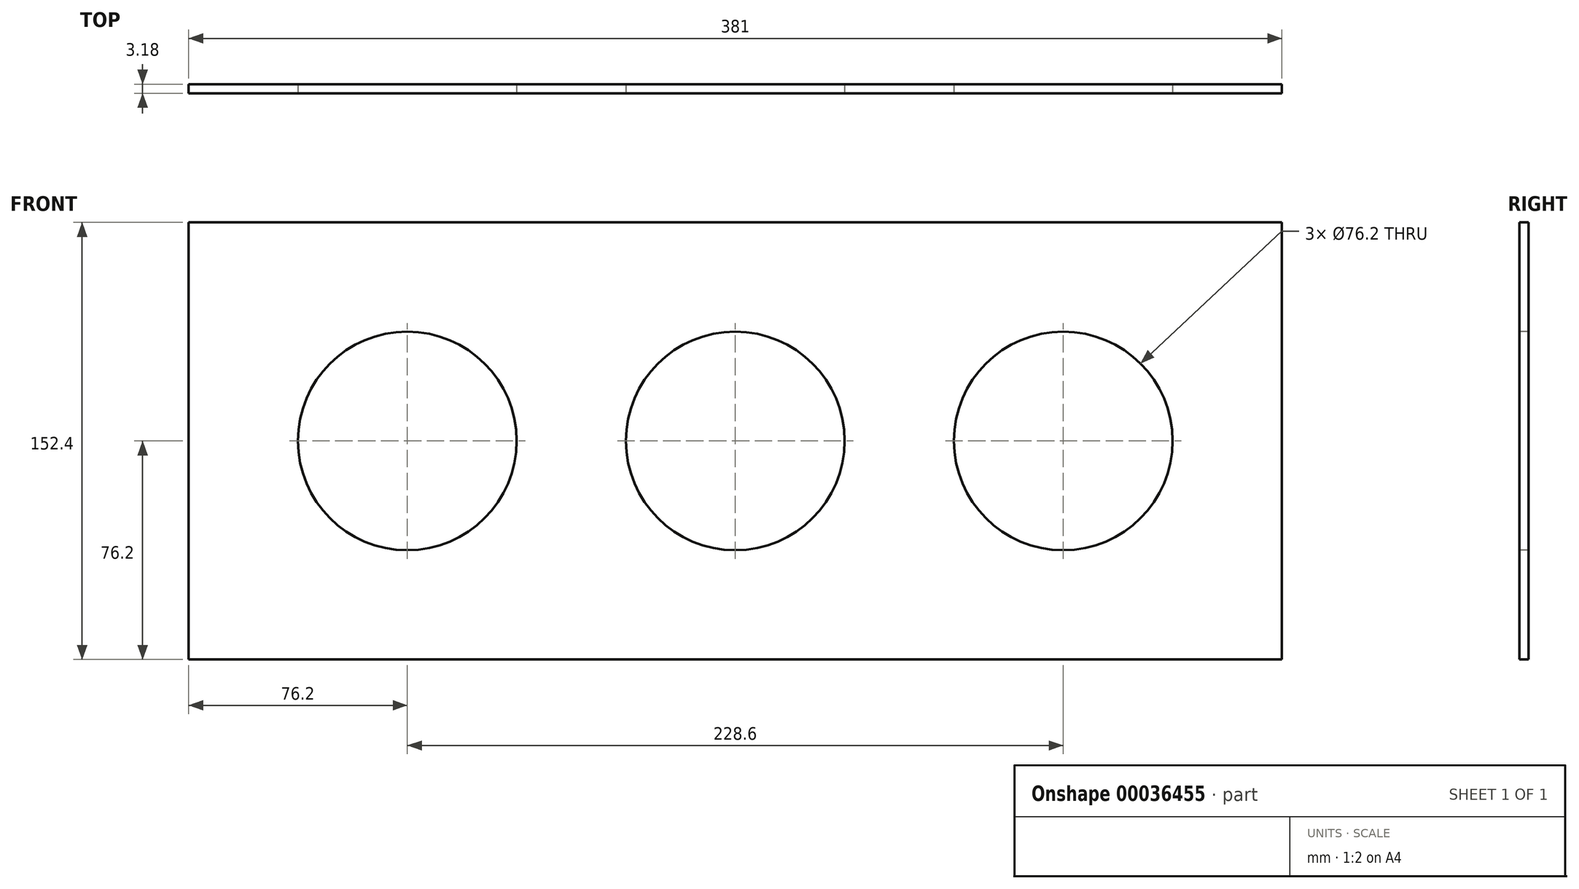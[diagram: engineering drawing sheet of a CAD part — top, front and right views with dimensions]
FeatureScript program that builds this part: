
annotation { "Feature Type Name" : "Feature", "Feature Type Description" : "" }
export const myFeature = defineFeature(function(context is Context, id is Id, definition is map)
    precondition{}
    {
        {
            var Q0;
            Q0=qCreatedBy(makeId("Front.planeOp"),FACE);
            var sketch = newSketch(context, id + "F0", { "sketchPlane" : qUnion([Q0])});
            skLineSegment(sketch, "E0.rect.bottom", {"start": v(190.5, 76.2) * mm, "end": v(-190.5, 76.2) * mm});
            skLineSegment(sketch, "E0.rect.top", {"start": v(190.5, -76.2) * mm, "end": v(-190.5, -76.2) * mm});
            skLineSegment(sketch, "E0.rect.left", {"start": v(190.5, 76.2) * mm, "end": v(190.5, -76.2) * mm});
            skLineSegment(sketch, "E0.rect.right", {"start": v(-190.5, 76.2) * mm, "end": v(-190.5, -76.2) * mm});
            skPoint(sketch, "E0.rect.middle", {"position": v(0, 0) * mm});
            skSolve(sketch);
        }
        {
            var Q0;
            Q0=makeQuery(id+"F0.imprint","IMPRINT",FACE,{"disambiguationData":[TD([[makeQuery(id+"F0.imprint","IMPRINT",EDGE,{"derivedFrom":sQuery(id+"F0.wireOp",EDGE,"E0.rect.bottom")}),1.0]])]});
            extrude(context, id + "F1", {"entities" : qUnion([Q0]), "endBound" : BoundingType.SYMMETRIC, "depth" : 3.17 * mm});
        }
        {
            var Q0;
            Q0=makeQuery(id+"F1.opExtrude","CAP_FACE",FACE,{"disambiguationData":[OSD([sQuery(id+"F0.wireOp",EDGE,"E0.rect.bottom"),sQuery(id+"F0.wireOp",EDGE,"E0.rect.top"),sQuery(id+"F0.wireOp",EDGE,"E0.rect.left"),sQuery(id+"F0.wireOp",EDGE,"E0.rect.right")])],"isStart":false});
            var sketch = newSketch(context, id + "F2", { "sketchPlane" : qUnion([Q0])});
            skCircle(sketch, "E1", {"center": v(0, 0) * mm, "radius": 38.1 * mm});
            skSolve(sketch);
        }
        {
            var Q0;
            Q0=makeQuery(id+"F2.imprint","IMPRINT",FACE,{"disambiguationData":[TD([[makeQuery(id+"F2.imprint","IMPRINT",EDGE,{"derivedFrom":sQuery(id+"F2.wireOp",EDGE,"E1")}),1.0]])]});
            var Q1;
            Q1=sQuery(id+"F2.wireOp",EDGE,"E1");
            extrude(context, id + "F3", {"entities" : qUnion([Q0]), "operationType" : NewBodyOperationType.REMOVE, "surfaceEntities" : qUnion([Q1]), "oppositeDirection" : true, "depth" : 3.17 * mm});
        }
        {
            var Q0;
            Q0=makeQuery(id+"F1.opExtrude","CAP_FACE",FACE,{"disambiguationData":[OSD([sQuery(id+"F0.wireOp",EDGE,"E0.rect.bottom"),sQuery(id+"F0.wireOp",EDGE,"E0.rect.top"),sQuery(id+"F0.wireOp",EDGE,"E0.rect.left"),sQuery(id+"F0.wireOp",EDGE,"E0.rect.right")])],"isStart":false});
            var sketch = newSketch(context, id + "F4", { "sketchPlane" : qUnion([Q0])});
            skCircle(sketch, "E2", {"center": v(-114.3, 0) * mm, "radius": 38.1 * mm});
            skSolve(sketch);
        }
        {
            var Q0;
            Q0=makeQuery(id+"F4.imprint","IMPRINT",FACE,{"disambiguationData":[TD([[makeQuery(id+"F4.imprint","IMPRINT",EDGE,{"derivedFrom":sQuery(id+"F4.wireOp",EDGE,"E2")}),1.0]])]});
            extrude(context, id + "F5", {"entities" : qUnion([Q0]), "operationType" : NewBodyOperationType.REMOVE, "oppositeDirection" : true, "depth" : 3.17 * mm});
        }
        {
            var Q0;
            Q0=makeQuery(id+"F1.opExtrude","CAP_FACE",FACE,{"disambiguationData":[OSD([sQuery(id+"F0.wireOp",EDGE,"E0.rect.bottom"),sQuery(id+"F0.wireOp",EDGE,"E0.rect.top"),sQuery(id+"F0.wireOp",EDGE,"E0.rect.left"),sQuery(id+"F0.wireOp",EDGE,"E0.rect.right")])],"isStart":false});
            var sketch = newSketch(context, id + "F6", { "sketchPlane" : qUnion([Q0])});
            skCircle(sketch, "E3", {"center": v(114.3, 0) * mm, "radius": 38.1 * mm});
            skSolve(sketch);
        }
        {
            var Q0;
            Q0=makeQuery(id+"F6.imprint","IMPRINT",FACE,{"disambiguationData":[TD([[makeQuery(id+"F6.imprint","IMPRINT",EDGE,{"derivedFrom":sQuery(id+"F6.wireOp",EDGE,"E3")}),1.0]])]});
            extrude(context, id + "F7", {"entities" : qUnion([Q0]), "operationType" : NewBodyOperationType.REMOVE, "oppositeDirection" : true, "depth" : 3.17 * mm});
        }
    });
